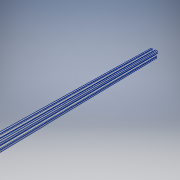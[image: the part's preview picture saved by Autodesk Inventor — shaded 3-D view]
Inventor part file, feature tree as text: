
AUTODESK INVENTOR PART (.ipt)
format: ipt  version: 2019 (Build 230136000, 136)  size: 396,800 bytes
history: native  units: in
note: dims shown in document units (in); Inventor stores cm internally (conversion verified against a paired STEP export)
features: extrude x3, sketch x3, other x1, plane x1, projected_geometry x1
ambient origin geometry x8: Origin, YZ Plane, XZ Plane, XY Plane, X Axis, Y Axis, Z Axis, Center Point
bodies: Solid1 (feature_tree)
feature tree (9):
  other  "Boss-Extrude1"
  extrude  "Extrusion1"  Depth=0.4375in
  plane  "Work Plane1"
  sketch  "Sketch6"  dims[d12=2.125in d13=0.25in]
  extrude  "Extrusion6"  Depth=0.25in
  extrude  "Extrusion7"  Depth=1.0in TaperAngle=0.0deg
  sketch  "Sketch1"  dims[d0=8.0in d1=0.0in d11=0.4375in]
  projected_geometry  "Projected Loop1"
  sketch  "Sketch7"  dims[d14=3.0in d17=1.0in d18=0.0in d19=1.0in d20=0.0in]
